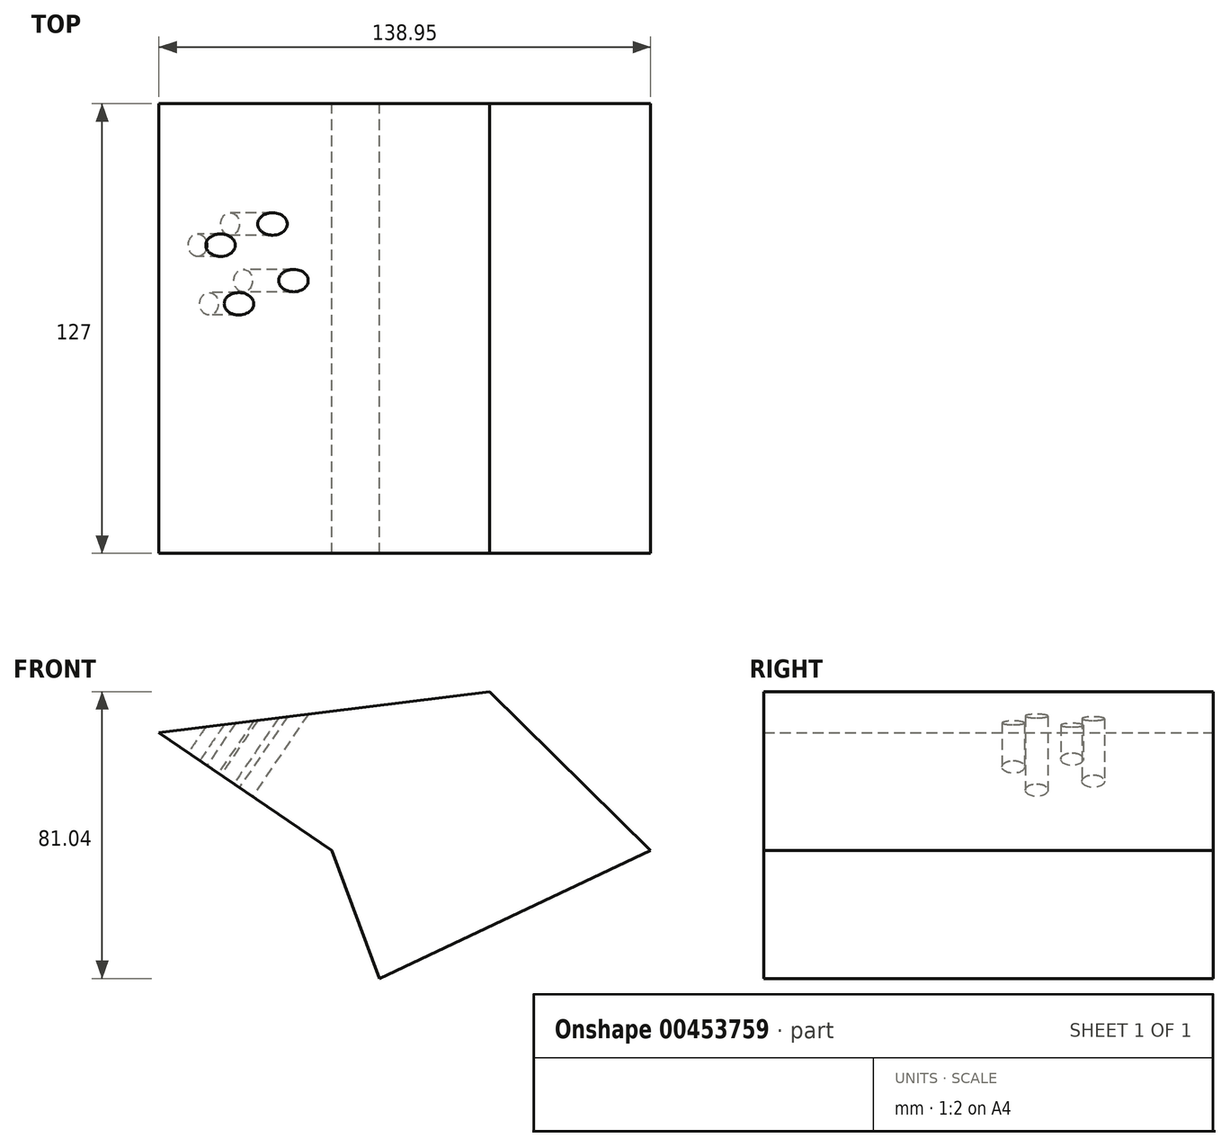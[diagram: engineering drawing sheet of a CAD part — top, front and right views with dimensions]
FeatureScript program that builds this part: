
annotation { "Feature Type Name" : "Feature", "Feature Type Description" : "" }
export const myFeature = defineFeature(function(context is Context, id is Id, definition is map)
    precondition{}
    {
        {
            var Q0;
            Q0=qCreatedBy(makeId("Front.planeOp"),FACE);
            var sketch = newSketch(context, id + "F0", { "sketchPlane" : qUnion([Q0])});
            skLineSegment(sketch, "E0", {"start": v(-98.33, 33.21) * mm, "end": v(-49.43, 0) * mm});
            skLineSegment(sketch, "E1", {"start": v(-49.43, 0) * mm, "end": v(-36, -36.16) * mm});
            skLineSegment(sketch, "E2", {"start": v(-36, -36.16) * mm, "end": v(40.62, 0) * mm});
            skLineSegment(sketch, "E3", {"start": v(40.62, 0) * mm, "end": v(-4.82, 44.88) * mm});
            skLineSegment(sketch, "E4", {"start": v(-4.82, 44.88) * mm, "end": v(-98.33, 33.21) * mm});
            skSolve(sketch);
        }
        {
            var Q0;
            Q0=makeQuery(id+"F0.imprint","IMPRINT",FACE,{"disambiguationData":[TD([[makeQuery(id+"F0.imprint","IMPRINT",EDGE,{"derivedFrom":sQuery(id+"F0.wireOp",EDGE,"E0")}),1.0]])]});
            extrude(context, id + "F1", {"entities" : qUnion([Q0]), "depth" : 127 * mm});
        }
        {
            var Q0;
            Q0=makeQuery(id+"F1.opExtrude","SWEPT_FACE",FACE,{"disambiguationData":[OSD([sQuery(id+"F0.wireOp",EDGE,"E0")])]});
            var sketch = newSketch(context, id + "F2", { "sketchPlane" : qUnion([Q0])});
            skLineSegment(sketch, "E5", {"start": v(-71.2, 49.93) * mm, "end": v(-75.68, 33.95) * mm});
            skLineSegment(sketch, "E6", {"start": v(-71.2, 49.93) * mm, "end": v(-82.87, 56.5) * mm});
            skLineSegment(sketch, "E7", {"start": v(-82.87, 56.5) * mm, "end": v(-86.8, 39.94) * mm});
            skLineSegment(sketch, "E8", {"start": v(-86.8, 39.94) * mm, "end": v(-75.68, 33.95) * mm});
            skSolve(sketch);
        }
        {
            var Q0;
            Q0=sQuery(id+"F2.wireOp",VERTEX,"E8.start");
            var Q1;
            Q1=sQuery(id+"F2.wireOp",VERTEX,"E6.start");
            var Q2;
            Q2=sQuery(id+"F2.wireOp",VERTEX,"E5.end");
            var Q3;
            Q3=sQuery(id+"F2.wireOp",VERTEX,"E7.start");
            var Q4;
            Q4=makeQuery(id+"F1.opExtrude","SWEPT_BODY",BODY,{"disambiguationData":[OSD([sQuery(id+"F0.wireOp",EDGE,"E0"),sQuery(id+"F0.wireOp",EDGE,"E1"),sQuery(id+"F0.wireOp",EDGE,"E2"),sQuery(id+"F0.wireOp",EDGE,"E3"),sQuery(id+"F0.wireOp",EDGE,"E4")])]});
            hole(context, id + "F3", {"style" : HoleStyle.SIMPLE, "endStyle" : HoleEndStyle.THROUGH, "holeDiameter" : 6.35 * mm, "isTappedThrough" : true, "tappedDepth" : 12.7 * mm, "tapClearance" : 3, "locations" : qUnion([Q0, Q1, Q2, Q3]), "scope" : qUnion([Q4])});
        }
    });
